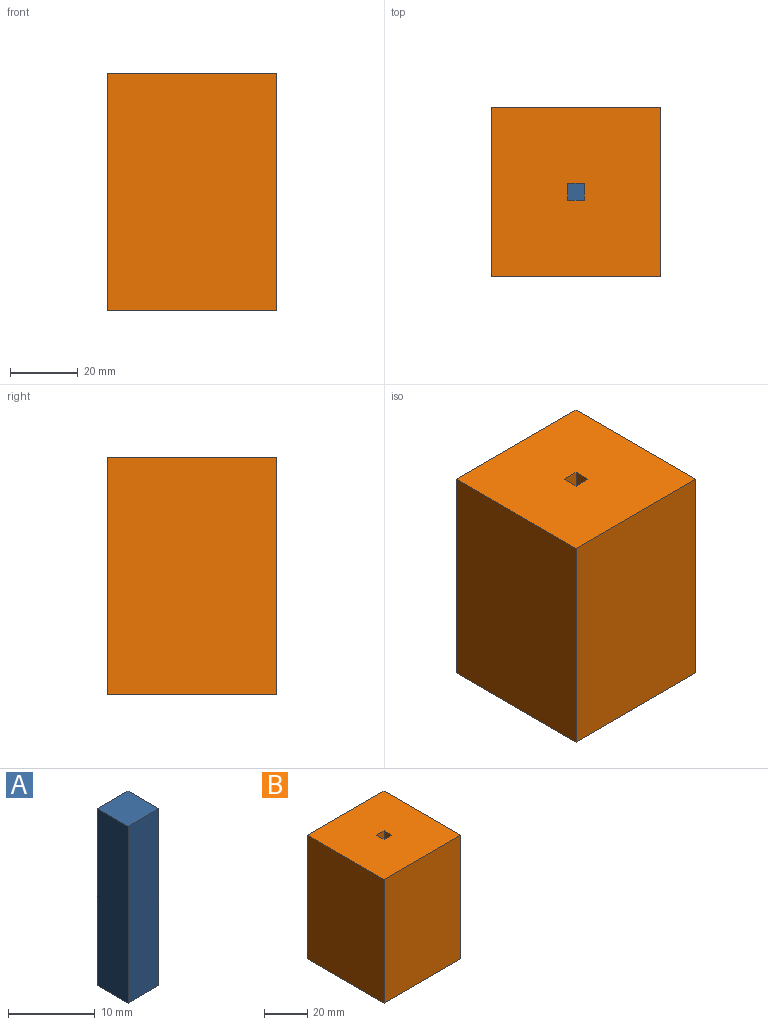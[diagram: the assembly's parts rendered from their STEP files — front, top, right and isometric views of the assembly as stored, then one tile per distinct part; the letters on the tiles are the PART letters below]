
ASSEMBLY  parts=2 mates=2
PART A: 6 faces, bbox 5x5x25 mm
  f0: plane 25x5mm, normal (-1,0,0), area 125mm2, adj f1,f3,f4,f5
  f1: plane 25x5mm, normal (0,-1,0), area 125mm2, adj f0,f2,f4,f5
  f2: plane 25x5mm, normal (1,0,0), area 125mm2, adj f1,f3,f4,f5
  f3: plane 25x5mm, normal (0,1,0), area 125mm2, adj f0,f2,f4,f5
  f4: plane 5x5mm, normal (0,0,1), area 25mm2, adj f0,f1,f2,f3
  f5: plane 5x5mm, normal (0,0,-1), area 25mm2, adj f0,f1,f2,f3
PART B: 10 faces, bbox 50x50x70 mm
  f0: plane 70x50mm, normal (-1,0,0), area 3500mm2, adj f1,f3,f4,f5
  f1: plane 70x50mm, normal (0,-1,0), area 3500mm2, adj f0,f2,f4,f5
  f2: plane 70x50mm, normal (1,0,0), area 3500mm2, adj f1,f3,f4,f5
  f3: plane 70x50mm, normal (0,1,0), area 3500mm2, adj f0,f2,f4,f5
  f4: plane 50x50mm, normal (0,0,1), area 2475mm2, adj f0,f1,f2,f3,f6,f7,f8,f9
  f5: plane 50x50mm, normal (0,0,-1), area 2475mm2, adj f0,f1,f2,f3,f6,f7,f8,f9
  f6: plane 70x5mm, normal (1,0,0), area 350mm2, adj f4,f5,f7,f9
  f7: plane 70x5mm, normal (0,1,0), area 350mm2, adj f4,f5,f6,f8
  f8: plane 70x5mm, normal (-1,0,0), area 350mm2, adj f4,f5,f7,f9
  f9: plane 70x5mm, normal (0,-1,0), area 350mm2, adj f4,f5,f6,f8
PLACE A t=(-21.25,22.74,43.99)mm
PLACE B t=(-21.25,22.74,3.99)mm fixed
MATE slider A.f4 <-> B.f4  axis (0,0,-1) through (-23.75,20.24,68.99)mm
MATE parallel B.f4 <-> A.f4  axis (0,0,1) through (-21.25,22.74,73.99)mm
